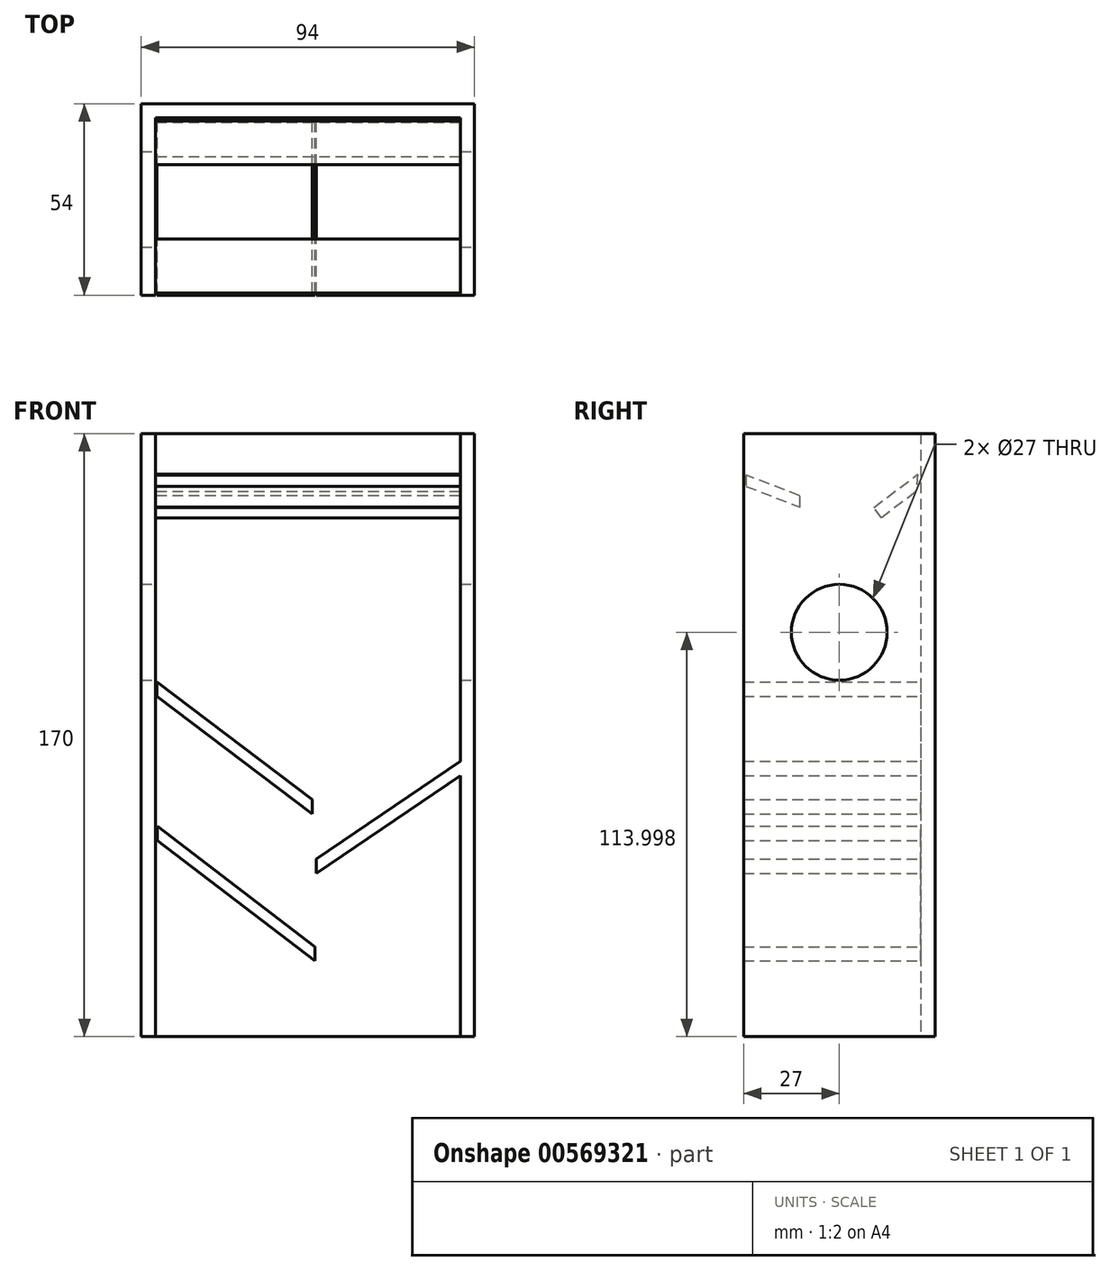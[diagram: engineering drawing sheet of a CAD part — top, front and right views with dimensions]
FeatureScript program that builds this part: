
annotation { "Feature Type Name" : "Feature", "Feature Type Description" : "" }
export const myFeature = defineFeature(function(context is Context, id is Id, definition is map)
    precondition{}
    {
        {
            var Q0;
            Q0=qCreatedBy(makeId("Front.planeOp"),FACE);
            var sketch = newSketch(context, id + "F0", { "sketchPlane" : qUnion([Q0])});
            skLineSegment(sketch, "E0", {"start": v(-34.06, 77.93) * mm, "end": v(-34.06, -92.07) * mm});
            skLineSegment(sketch, "E1", {"start": v(-34.06, 77.93) * mm, "end": v(55.94, 77.93) * mm});
            skLineSegment(sketch, "E2", {"start": v(55.94, 77.93) * mm, "end": v(55.94, -92.07) * mm});
            skLineSegment(sketch, "E3", {"start": v(55.94, -92.07) * mm, "end": v(-34.06, -92.07) * mm});
            skSolve(sketch);
        }
        {
            var Q0;
            Q0=qSketchRegion(id+"F0",true);
            extrude(context, id + "F1", {"entities" : qUnion([Q0]), "depth" : 4 * mm});
        }
        {
            var Q0;
            Q0=makeQuery(id+"F1.opExtrude","SWEPT_FACE",FACE,{"disambiguationData":[OSD([sQuery(id+"F0.wireOp",EDGE,"E2")])]});
            var sketch = newSketch(context, id + "F2", { "sketchPlane" : qUnion([Q0])});
            skLineSegment(sketch, "E4", {"start": v(0, 77.93) * mm, "end": v(0, -92.07) * mm});
            skLineSegment(sketch, "E5", {"start": v(0, 77.93) * mm, "end": v(-54, 77.93) * mm});
            skLineSegment(sketch, "E6", {"start": v(-54, 77.93) * mm, "end": v(-54, -92.07) * mm});
            skLineSegment(sketch, "E7", {"start": v(-54, -92.07) * mm, "end": v(0, -92.07) * mm});
            skSolve(sketch);
        }
        {
            var Q0;
            {var subQ2=sQuery(id+"F2.wireOp",EDGE,"E6");Q0=makeQuery(id+"F2.imprint","IMPRINT",FACE,{"disambiguationData":[TD([[makeQuery(id+"F2.imprint","IMPRINT",EDGE,{"derivedFrom":subQ2}),1.0]])]});}
            extrude(context, id + "F3", {"entities" : qUnion([Q0]), "operationType" : NewBodyOperationType.ADD, "oppositeDirection" : true, "depth" : 4 * mm});
        }
        {
            var Q0;
            Q0=makeQuery(id+"F1.opExtrude","SWEPT_FACE",FACE,{"disambiguationData":[OSD([sQuery(id+"F0.wireOp",EDGE,"E0")])]});
            var sketch = newSketch(context, id + "F4", { "sketchPlane" : qUnion([Q0])});
            skLineSegment(sketch, "E8", {"start": v(0, 77.93) * mm, "end": v(0, -92.07) * mm});
            skLineSegment(sketch, "E9", {"start": v(0, -92.07) * mm, "end": v(54, -92.07) * mm});
            skLineSegment(sketch, "E10", {"start": v(0, 77.93) * mm, "end": v(54, 77.93) * mm});
            skLineSegment(sketch, "E11", {"start": v(54, 77.93) * mm, "end": v(54, -92.07) * mm});
            skSolve(sketch);
        }
        {
            var Q0;
            {var subQ2=sQuery(id+"F4.wireOp",EDGE,"E11");Q0=makeQuery(id+"F4.imprint","IMPRINT",FACE,{"disambiguationData":[TD([[makeQuery(id+"F4.imprint","IMPRINT",EDGE,{"derivedFrom":subQ2}),-1.0]])]});}
            extrude(context, id + "F5", {"entities" : qUnion([Q0]), "depth" : 4 * mm});
        }
        {
            var Q0;
            Q0=makeQuery(id+"F5.opExtrude","SWEPT_FACE",FACE,{"disambiguationData":[OSD([sQuery(id+"F0.wireOp",EDGE,"E0")])]});
            extrude(context, id + "F6", {"entities" : qUnion([Q0]), "depth" : 4 * mm});
        }
        {
            var Q0;
            Q0=makeQuery(id+"F1.opExtrude","SWEPT_BODY",BODY,{"disambiguationData":[OSD([sQuery(id+"F0.wireOp",EDGE,"E0"),sQuery(id+"F0.wireOp",EDGE,"E1"),sQuery(id+"F0.wireOp",EDGE,"E2"),sQuery(id+"F0.wireOp",EDGE,"E3")])]});
            var Q1;
            Q1=makeQuery(id+"F6.opExtrude","SWEPT_BODY",BODY,{"disambiguationData":[OSD([sQuery(id+"F0.wireOp",EDGE,"E0")])]});
            var Q2;
            Q2=makeQuery(id+"F5.opExtrude","SWEPT_BODY",BODY,{"disambiguationData":[OSD([sQuery(id+"F0.wireOp",EDGE,"E0"),sQuery(id+"F4.wireOp",EDGE,"E9"),sQuery(id+"F4.wireOp",EDGE,"E10"),sQuery(id+"F4.wireOp",EDGE,"E11")])]});
            booleanBodies(context, id + "F7", {"operationType" : BooleanOperationType.UNION, "tools" : qUnion([Q0, Q1, Q2])});
        }
        {
            var Q0;
            {var subQ0=sQuery(id+"F0.wireOp",EDGE,"E2");Q0=makeQuery(id+"F3.boolean.opBoolean","MERGE",FACE,{"derivedFrom":[makeQuery(id+"F1.opExtrude","SWEPT_FACE",FACE,{"disambiguationData":[OSD([subQ0])]}),makeQuery(id+"F3.opExtrude","CAP_FACE",FACE,{"disambiguationData":[OSD([subQ0,sQuery(id+"F2.wireOp",EDGE,"E5"),sQuery(id+"F2.wireOp",EDGE,"E6"),sQuery(id+"F2.wireOp",EDGE,"E7")])],"isStart":true})]});}
            var sketch = newSketch(context, id + "F8", { "sketchPlane" : qUnion([Q0])});
            skLineSegment(sketch, "E12", {"start": v(-27, 102) * mm, "end": v(-27, -107.35) * mm, "construction": true});
            skPoint(sketch, "E12.startSnap0", {"position": v(-27, 77.93) * mm});
            skLineSegment(sketch, "E13", {"start": v(-27, 21.93) * mm, "end": v(-79.39, 21.93) * mm, "construction": true});
            skSolve(sketch);
        }
        {
            var Q0;
            Q0=sQuery(id+"F8.wireOp",VERTEX,"E13.start");
            var Q1;
            Q1=makeQuery(id+"F1.opExtrude","SWEPT_BODY",BODY,{"disambiguationData":[OSD([sQuery(id+"F0.wireOp",EDGE,"E0"),sQuery(id+"F0.wireOp",EDGE,"E1"),sQuery(id+"F0.wireOp",EDGE,"E2"),sQuery(id+"F0.wireOp",EDGE,"E3")])]});
            hole(context, id + "F9", {"style" : HoleStyle.SIMPLE, "endStyle" : HoleEndStyle.THROUGH, "holeDiameter" : 27 * mm, "majorDiameter" : 5 * mm, "isTappedThrough" : true, "tappedDepth" : 12 * mm, "tapClearance" : 3, "locations" : qUnion([Q0]), "scope" : qUnion([Q1])});
        }
        {
            var Q0;
            Q0=makeQuery(id+"F3.opExtrude","CAP_FACE",FACE,{"disambiguationData":[OSD([sQuery(id+"F0.wireOp",EDGE,"E2"),sQuery(id+"F2.wireOp",EDGE,"E5"),sQuery(id+"F2.wireOp",EDGE,"E6"),sQuery(id+"F2.wireOp",EDGE,"E7")])],"isStart":false});
            var sketch = newSketch(context, id + "F10", { "sketchPlane" : qUnion([Q0])});
            skLineSegment(sketch, "E14", {"start": v(29, 77.93) * mm, "end": v(29, -92.07) * mm, "construction": true});
            skLineSegment(sketch, "E15", {"start": v(4, -38.07) * mm, "end": v(144.45, -38.07) * mm, "construction": true});
            skLineSegment(sketch, "E16", {"start": v(4, -77.07) * mm, "end": v(155.7, -77.07) * mm, "construction": true});
            skLineSegment(sketch, "E17", {"start": v(54, -38.07) * mm, "end": v(54, -34.07) * mm, "construction": true});
            skLineSegment(sketch, "E18", {"start": v(54, -34.07) * mm, "end": v(4, -34.07) * mm});
            skLineSegment(sketch, "E19", {"start": v(4, -34.07) * mm, "end": v(4, -38.07) * mm});
            skLineSegment(sketch, "E20", {"start": v(54, -38.07) * mm, "end": v(4, -38.07) * mm});
            skLineSegment(sketch, "E21", {"start": v(54, -38.07) * mm, "end": v(54, -9.79) * mm});
            skSolve(sketch);
        }
        {
            var Q0;
            {var subQ0=sQuery(id+"F0.wireOp",EDGE,"E0");Q0=makeQuery(id+"F7.opBoolean","MERGE",FACE,{"derivedFrom":[makeQuery(id+"F5.opExtrude","CAP_FACE",FACE,{"disambiguationData":[OSD([subQ0,sQuery(id+"F4.wireOp",EDGE,"E9"),sQuery(id+"F4.wireOp",EDGE,"E10"),sQuery(id+"F4.wireOp",EDGE,"E11")])],"isStart":true}),makeQuery(id+"F6.opExtrude","SWEPT_FACE",FACE,{"disambiguationData":[OSD([subQ0]),TDD([makeQuery(id+"F5.opExtrude","CAP_EDGE",EDGE,{"disambiguationData":[OSD([subQ0])],"isStart":true})])]})]});}
            var sketch = newSketch(context, id + "F11", { "sketchPlane" : qUnion([Q0])});
            skLineSegment(sketch, "E22", {"start": v(-29, 77.93) * mm, "end": v(-29, -92.07) * mm, "construction": true});
            skLineSegment(sketch, "E23", {"start": v(-4, -19.07) * mm, "end": v(-83.45, -19.07) * mm, "construction": true});
            skLineSegment(sketch, "E24", {"start": v(-4, -58.07) * mm, "end": v(-95.37, -58.07) * mm, "construction": true});
            skSolve(sketch);
        }
        {
            var Q0;
            {var subQ3=sQuery(id+"F4.wireOp",EDGE,"E11");Q0=makeQuery(id+"F11.imprint","IMPRINT",FACE,{"disambiguationData":[TD([[makeQuery(id+"F11.imprint","IMPRINT",EDGE,{"derivedFrom":makeQuery(id+"F5.opExtrude","CAP_EDGE",EDGE,{"disambiguationData":[OSD([subQ3])],"isStart":true})}),1.0]])]});}
            var sketch = newSketch(context, id + "F12", { "sketchPlane" : qUnion([Q0])});
            skLineSegment(sketch, "E25", {"start": v(-53.34, 66.27) * mm, "end": v(-38.14, 60.4) * mm});
            skLineSegment(sketch, "E26", {"start": v(-38.14, 60.4) * mm, "end": v(-38.14, 57.23) * mm});
            skLineSegment(sketch, "E27", {"start": v(-38.14, 57.23) * mm, "end": v(-53.34, 63.1) * mm});
            skLineSegment(sketch, "E28", {"start": v(-53.34, 63.1) * mm, "end": v(-53.34, 66.27) * mm});
            skSolve(sketch);
        }
        {
            var Q0;
            Q0=makeQuery(id+"F12.imprint","IMPRINT",FACE,{"disambiguationData":[TD([[makeQuery(id+"F12.imprint","IMPRINT",EDGE,{"derivedFrom":sQuery(id+"F12.wireOp",EDGE,"E25")}),-1.0]])]});
            extrude(context, id + "F13", {"entities" : qUnion([Q0]), "operationType" : NewBodyOperationType.ADD, "depth" : 88.2 * mm, "offsetDistance" : 25 * mm});
        }
        {
            var Q0;
            {var subQ3=sQuery(id+"F4.wireOp",EDGE,"E11");Q0=makeQuery(id+"F11.imprint","IMPRINT",FACE,{"disambiguationData":[TD([[makeQuery(id+"F11.imprint","IMPRINT",EDGE,{"derivedFrom":makeQuery(id+"F5.opExtrude","CAP_EDGE",EDGE,{"disambiguationData":[OSD([subQ3])],"isStart":true})}),1.0]])]});}
            var sketch = newSketch(context, id + "F14", { "sketchPlane" : qUnion([Q0])});
            skLineSegment(sketch, "E29", {"start": v(-4.9, 66.47) * mm, "end": v(-16.15, 57.98) * mm});
            skLineSegment(sketch, "E30", {"start": v(-16.15, 57.98) * mm, "end": v(-13.95, 55.06) * mm});
            skLineSegment(sketch, "E31", {"start": v(-13.95, 55.06) * mm, "end": v(-5.46, 61.47) * mm});
            skLineSegment(sketch, "E32", {"start": v(-5.46, 61.47) * mm, "end": v(-4.9, 66.47) * mm});
            skSolve(sketch);
        }
        {
            var Q0;
            Q0=makeQuery(id+"F14.imprint","IMPRINT",FACE,{"disambiguationData":[TD([[makeQuery(id+"F14.imprint","IMPRINT",EDGE,{"derivedFrom":sQuery(id+"F14.wireOp",EDGE,"E29")}),1.0]])]});
            extrude(context, id + "F15", {"entities" : qUnion([Q0]), "operationType" : NewBodyOperationType.ADD, "depth" : 87.7 * mm, "offsetDistance" : 25 * mm});
        }
        {
            var Q0;
            Q0=makeQuery(id+"F15.opExtrude","SWEPT_FACE",FACE,{"disambiguationData":[OSD([sQuery(id+"F14.wireOp",EDGE,"E30")])]});
            extrude(context, id + "F16", {"entities" : qUnion([Q0]), "operationType" : NewBodyOperationType.ADD, "depth" : 1.4 * mm, "offsetDistance" : 25 * mm});
        }
        {
            var Q0;
            Q0=makeQuery(id+"F1.opExtrude","CAP_FACE",FACE,{"disambiguationData":[OSD([sQuery(id+"F0.wireOp",EDGE,"E0"),sQuery(id+"F0.wireOp",EDGE,"E1"),sQuery(id+"F0.wireOp",EDGE,"E2"),sQuery(id+"F0.wireOp",EDGE,"E3")])],"isStart":false});
            var sketch = newSketch(context, id + "F17", { "sketchPlane" : qUnion([Q0])});
            skLineSegment(sketch, "E33.0.0", {"start": v(51.94, -92.07) * mm, "end": v(51.94, 77.93) * mm});
            skLineSegment(sketch, "E33.0.1", {"start": v(51.94, 77.93) * mm, "end": v(-34.06, 77.93) * mm});
            skLineSegment(sketch, "E33.0.2", {"start": v(-34.06, 77.93) * mm, "end": v(-34.06, -92.07) * mm});
            skLineSegment(sketch, "E33.0.3", {"start": v(-34.06, -92.07) * mm, "end": v(51.94, -92.07) * mm});
            skLineSegment(sketch, "E34.0.0", {"start": v(-34.06, -92.07) * mm, "end": v(-34.06, 77.93) * mm, "construction": true});
            skLineSegment(sketch, "E34.0.1", {"start": v(-34.06, 77.93) * mm, "end": v(-38.06, 77.93) * mm, "construction": true});
            skLineSegment(sketch, "E34.0.2", {"start": v(-38.06, 77.93) * mm, "end": v(-38.06, -92.07) * mm, "construction": true});
            skLineSegment(sketch, "E34.0.3", {"start": v(-38.06, -92.07) * mm, "end": v(-34.06, -92.07) * mm, "construction": true});
            skLineSegment(sketch, "E35.0.2", {"start": v(-34.06, 77.93) * mm, "end": v(-34.06, -92.07) * mm, "construction": true});
            skLineSegment(sketch, "E36", {"start": v(-34.06, 77.93) * mm, "end": v(10.94, 77.93) * mm, "construction": true});
            skLineSegment(sketch, "E37", {"start": v(10.94, 77.93) * mm, "end": v(10.94, -92.07) * mm, "construction": true});
            skSolve(sketch);
        }
        {
            var Q0;
            Q0=makeQuery(id+"F17.imprint","IMPRINT",FACE,{"disambiguationData":[TD([[makeQuery(id+"F17.imprint","IMPRINT",EDGE,{"derivedFrom":sQuery(id+"F17.wireOp",EDGE,"E33.0.0")}),-1.0]])]});
            var sketch = newSketch(context, id + "F18", { "sketchPlane" : qUnion([Q0])});
            skLineSegment(sketch, "E38", {"start": v(5.65, 102.74) * mm, "end": v(5.65, -22.26) * mm, "construction": true});
            skLineSegment(sketch, "E39", {"start": v(5.65, -22.26) * mm, "end": v(-32.54, -22.26) * mm, "construction": true});
            skSolve(sketch);
        }
        {
            var Q0;
            Q0=makeQuery(id+"F17.imprint","IMPRINT",FACE,{"disambiguationData":[TD([[makeQuery(id+"F17.imprint","IMPRINT",EDGE,{"derivedFrom":sQuery(id+"F17.wireOp",EDGE,"E33.0.0")}),-1.0]])]});
            var sketch = newSketch(context, id + "F19", { "sketchPlane" : qUnion([Q0])});
            skLineSegment(sketch, "E40", {"start": v(-30.56, 7.95) * mm, "end": v(-33.6, 7.95) * mm, "construction": true});
            skLineSegment(sketch, "E41", {"start": v(-33.6, 7.95) * mm, "end": v(5.59, 7.95) * mm, "construction": true});
            skSolve(sketch);
        }
        {
            var Q0;
            Q0=makeQuery(id+"F19.imprint","IMPRINT",FACE,{"disambiguationData":[TD([[makeQuery(id+"F19.imprint","IMPRINT",EDGE,{"derivedFrom":makeQuery(id+"F17.imprint","IMPRINT",EDGE,{"derivedFrom":sQuery(id+"F17.wireOp",EDGE,"E33.0.0")})}),-1.0]])]});
            var sketch = newSketch(context, id + "F20", { "sketchPlane" : qUnion([Q0])});
            skLineSegment(sketch, "E42", {"start": v(-33.63, 7.92) * mm, "end": v(10.22, -25.28) * mm});
            skLineSegment(sketch, "E43", {"start": v(-33.63, 7.92) * mm, "end": v(-33.63, 3.92) * mm});
            skLineSegment(sketch, "E44", {"start": v(-33.63, 3.92) * mm, "end": v(10.22, -29.28) * mm});
            skLineSegment(sketch, "E45", {"start": v(10.22, -29.28) * mm, "end": v(10.22, -25.28) * mm});
            skSolve(sketch);
        }
        {
            var Q0;
            Q0=makeQuery(id+"F20.imprint","IMPRINT",FACE,{"disambiguationData":[TD([[makeQuery(id+"F20.imprint","IMPRINT",EDGE,{"derivedFrom":sQuery(id+"F20.wireOp",EDGE,"E42")}),-1.0]])]});
            extrude(context, id + "F21", {"entities" : qUnion([Q0]), "operationType" : NewBodyOperationType.ADD, "depth" : 50 * mm, "offsetDistance" : 25 * mm});
        }
        {
            var Q0;
            Q0=makeQuery(id+"F19.imprint","IMPRINT",FACE,{"disambiguationData":[TD([[makeQuery(id+"F19.imprint","IMPRINT",EDGE,{"derivedFrom":makeQuery(id+"F17.imprint","IMPRINT",EDGE,{"derivedFrom":sQuery(id+"F17.wireOp",EDGE,"E33.0.0")})}),-1.0]])]});
            var sketch = newSketch(context, id + "F22", { "sketchPlane" : qUnion([Q0])});
            skLineSegment(sketch, "E46", {"start": v(55.55, -12) * mm, "end": v(55.55, -42) * mm, "construction": true});
            skLineSegment(sketch, "E47", {"start": v(55.55, -42) * mm, "end": v(11.25, -42) * mm, "construction": true});
            skLineSegment(sketch, "E48", {"start": v(55.55, -12) * mm, "end": v(11.25, -42) * mm});
            skLineSegment(sketch, "E49", {"start": v(55.55, -12) * mm, "end": v(55.55, -16) * mm});
            skLineSegment(sketch, "E50", {"start": v(55.55, -16) * mm, "end": v(11.25, -46) * mm});
            skLineSegment(sketch, "E51", {"start": v(11.25, -46) * mm, "end": v(11.25, -42) * mm});
            skSolve(sketch);
        }
        {
            var Q0;
            Q0=qSketchRegion(id+"F22",true);
            extrude(context, id + "F23", {"entities" : qUnion([Q0]), "operationType" : NewBodyOperationType.ADD, "depth" : 50 * mm, "offsetDistance" : 25 * mm});
        }
        {
            var Q0;
            Q0=makeQuery(id+"F18.imprint","IMPRINT",FACE,{"disambiguationData":[TD([[makeQuery(id+"F18.imprint","IMPRINT",EDGE,{"derivedFrom":makeQuery(id+"F17.imprint","IMPRINT",EDGE,{"derivedFrom":sQuery(id+"F17.wireOp",EDGE,"E33.0.0")})}),-1.0]])]});
            var sketch = newSketch(context, id + "F24", { "sketchPlane" : qUnion([Q0])});
            skLineSegment(sketch, "E52", {"start": v(5.7, -32.73) * mm, "end": v(5.7, -62.73) * mm, "construction": true});
            skLineSegment(sketch, "E53", {"start": v(5.7, -62.73) * mm, "end": v(-33.49, -62.73) * mm, "construction": true});
            skLineSegment(sketch, "E54", {"start": v(-33.49, -62.73) * mm, "end": v(-33.49, -32.73) * mm, "construction": true});
            skLineSegment(sketch, "E55", {"start": v(-33.49, -32.73) * mm, "end": v(5.7, -32.73) * mm, "construction": true});
            skLineSegment(sketch, "E56", {"start": v(-33.49, -32.73) * mm, "end": v(5.7, -62.73) * mm});
            skLineSegment(sketch, "E57", {"start": v(5.7, -66.73) * mm, "end": v(-33.49, -36.73) * mm});
            skLineSegment(sketch, "E58", {"start": v(-33.49, -36.73) * mm, "end": v(-33.49, -32.73) * mm});
            skLineSegment(sketch, "E59", {"start": v(5.7, -62.73) * mm, "end": v(-33.49, -32.73) * mm, "construction": true});
            skLineSegment(sketch, "E60", {"start": v(-33.49, -32.73) * mm, "end": v(10.92, -66.73) * mm, "construction": true});
            skLineSegment(sketch, "E61", {"start": v(10.92, -66.73) * mm, "end": v(10.92, -70.73) * mm});
            skLineSegment(sketch, "E62", {"start": v(10.92, -70.73) * mm, "end": v(5.7, -66.73) * mm});
            skLineSegment(sketch, "E63", {"start": v(-33.49, -32.73) * mm, "end": v(10.92, -66.73) * mm});
            skLineSegment(sketch, "E64", {"start": v(10.92, -70.73) * mm, "end": v(-33.49, -36.73) * mm});
            skSolve(sketch);
        }
        {
            var Q0;
            Q0=qSketchRegion(id+"F24",true);
            extrude(context, id + "F25", {"entities" : qUnion([Q0]), "operationType" : NewBodyOperationType.ADD, "depth" : 50 * mm, "offsetDistance" : 25 * mm});
        }
    });
